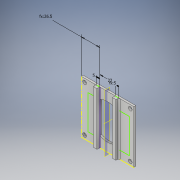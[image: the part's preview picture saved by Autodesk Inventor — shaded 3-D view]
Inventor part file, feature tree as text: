
AUTODESK INVENTOR PART (.ipt)
format: ipt  version: 2019 (Build 230136000, 136)  size: 162,816 bytes
history: native  units: mm
features: extrude x3, other x2, sketch x2, plane x1, mirror x1, fillet x1
ambient origin geometry x8: Origin, YZ Plane, XZ Plane, XY Plane, X Axis, Y Axis, Z Axis, Center Point
bodies: Body1 (feature_tree), Body2 (feature_tree), Body3 (feature_tree)
feature tree (10):
  other  "50x5 interface.ipt"
  extrude  "Extrusion1"  Depth=2.8mm TaperAngle=0.0deg
  sketch  "Sketch3"  dims[d4=5.0mm d5=2.8mm d6=0.0mm d7=4.0mm d8=0.0mm d9=90.0deg d11=26.5mm d13=5.0mm d14=22.0mm d15=4.0mm d16=0.0mm d17=2.0mm]
  extrude  "Extrusion2"  Depth=2.8mm TaperAngle=0.0deg
  plane  "Work Plane2"
  mirror  "Mirror1"
  extrude  "Extrusion3"  Depth=4.0mm TaperAngle=0.0deg
  fillet  "Fillet1"  [1 undecoded]
  sketch  "Sketch1"  dims[d1=10.0mm d2=2.8mm d3=0.0mm]
  other  "Work Axis1"
note: 1 required parameter value undecoded (feature->parameter linkage not recoverable at this tier; creation-order binding heuristic only, values carry confidence <= 0.55)
